# Revit family: 795310001_Griferia Marruecos a Pared
name_source: partatom
category: Plumbing Fixtures
units: mm (PartAtom-declared; Revit-internal decimal feet)

## family parameters
Always vertical = Yes
Cut with Voids When Loaded = No
Host = Wall
OmniClass Number = 23.31.11.00
OmniClass Title = Faucets
Part Type = Normal
Room Calculation Point = No
Round Connector Dimension = Use Diameter
Shared = No

## types (1)
- Type 1
    Alto = 134 mm  [stored 0.439633 ft]
    Ancho = 87 mm  [stored 0.285433 ft]
    Capacidad de flujo máximo por norma = 80 Psi: 8,3 L/min.
    Ciclo de vida de la unidad de cierre = 500.000 ciclos.
    Creado por = BIMBAU
    Cuidado Y Limpieza = Los acabados superﬁciales son aquellos que le imprimen una apariencia
especial y estética a su producto y además le brindan protección. Para
prolongar sus cualidades es vital que la limpieza profunda del producto se
haga únicamente con agua y jabón suave y que en el secado y el brillo se
utilice un paño de algodón limpio; dicha limpieza se recomienda 2 veces a
la semana y en zonas costeras a diario por la salinidad del ambiente. Por
ningún motivo deben usarse elementos abrasivos, ácidos o disolventes
para la limpieza del producto. Los acabados pueden variar su
comportamiento en zonas costeras y/o en ambientes corrosivos
    Default Elevation = 0 mm  [stored 0 ft]
    Description = El lavaplatos sencillo de pared Marruecos ha sido diseñada para trabajar en perfecta armonía
con el espacio; inspirada en las necesidades del consumidor latinoamericano
dando como resultado un producto robusto y funcional. Permite regular la temperatura
del agua con una sola manija. Incorpora un sistema de aireador que genera un chorro de
agua espumoso, agradable al tacto.
    Fecha de creación = 5/11/2021
    Garantía = 30 Años
    Manufacturer = Corona - Grival
    Material = Corona_Plastico_Cromado
    Model = Griferia Marruecos a Pared
    Peso Bruto aprox = 580gr. / 1,28Lb.
    Peso Neto aprox = 520gr. / 1,15Lb.
    Presión máxima recomendada = 125 psi.
    Presión mínima recomendada = 20 psi.
    Profundidad = 218 mm  [stored 0.715223 ft]
    Recubrimientos = Resistente a la corrosión, pelado y decoloración por agua. Recubrimientos no tóxicos
    Referencia = 795310001
    Temperaturas máxima de trabajo = 71 ºC / 159,8 ºF.
    Temperaturas mínima de trabajo = 5 ºC / 41 ºF.
    Uso = Doméstico

note: [stored X ft] marks values corroborated as IEEE doubles in the binary element streams (Revit-internal decimal feet)

## geometry (parser evidence)
native form markers: Sweep x6
no freeform markers — native parametric forms only
